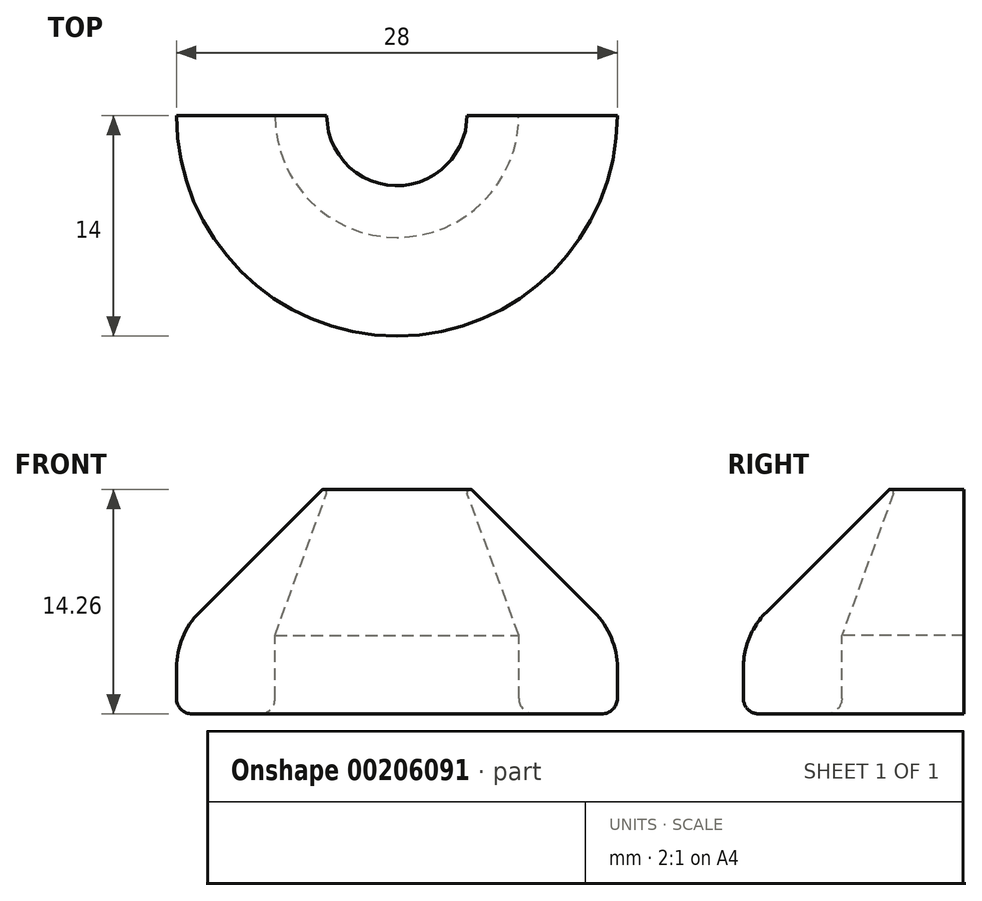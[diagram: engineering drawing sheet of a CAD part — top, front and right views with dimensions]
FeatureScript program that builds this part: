
annotation { "Feature Type Name" : "Feature", "Feature Type Description" : "" }
export const myFeature = defineFeature(function(context is Context, id is Id, definition is map)
    precondition{}
    {
        {
            var Q0;
            Q0=qCreatedBy(makeId("Front.planeOp"),FACE);
            var sketch = newSketch(context, id + "F0", { "sketchPlane" : qUnion([Q0])});
            skLineSegment(sketch, "E0", {"start": v(0, 30) * mm, "end": v(0, -30) * mm, "construction": true});
            skLineSegment(sketch, "E1", {"start": v(0, -30) * mm, "end": v(7.64, -30) * mm, "construction": true});
            skLineSegment(sketch, "E2", {"start": v(7.64, -30) * mm, "end": v(7.64, -25) * mm, "construction": true});
            skLineSegment(sketch, "E3", {"start": v(7.64, -25) * mm, "end": v(4, -15) * mm, "construction": true});
            skLineSegment(sketch, "E4", {"start": v(4, -15) * mm, "end": v(4, 0) * mm, "construction": true});
            skLineSegment(sketch, "E5", {"start": v(4, 0) * mm, "end": v(4, 15) * mm, "construction": true});
            skLineSegment(sketch, "E6", {"start": v(4, 15) * mm, "end": v(7.64, 25) * mm, "construction": true});
            skLineSegment(sketch, "E7", {"start": v(7.64, 25) * mm, "end": v(7.64, 30) * mm, "construction": true});
            skLineSegment(sketch, "E8", {"start": v(7.64, 30) * mm, "end": v(0, 30) * mm, "construction": true});
            skLineSegment(sketch, "E9", {"start": v(4, -15) * mm, "end": v(14, -25) * mm});
            skLineSegment(sketch, "E10", {"start": v(14, -25) * mm, "end": v(14, -30) * mm});
            skLineSegment(sketch, "E11", {"start": v(14, -30) * mm, "end": v(7.64, -30) * mm});
            skLineSegment(sketch, "E12", {"start": v(7.74, -30) * mm, "end": v(7.74, -25) * mm});
            skLineSegment(sketch, "E13", {"start": v(7.74, -25) * mm, "end": v(4.16, -15.16) * mm});
            skSolve(sketch);
        }
        {
            var Q0;
            Q0=qSketchRegion(id+"F0",true);
            var Q1;
            Q1=sQuery(id+"F0.wireOp",EDGE,"E0");
            revolve(context, id + "F1", {"entities" : qUnion([Q0]), "axis" : qUnion([Q1]), "revolveType" : RevolveType.ONE_DIRECTION, "angle" : 180 * degree});
        }
        {
            var Q0;
            Q0=makeQuery(id+"F1.opRevolve","SWEPT_EDGE",EDGE,{"disambiguationData":[OSD([sQuery(id+"F0.wireOp",EDGE,"E6"),sQuery(id+"F0.wireOp",EDGE,"E7")])]});
            var Q1;
            Q1=makeQuery(id+"F1.opRevolve","SWEPT_EDGE",EDGE,{"disambiguationData":[OSD([sQuery(id+"F0.wireOp",EDGE,"E2"),sQuery(id+"F0.wireOp",EDGE,"E3")])]});
            var Q2;
            Q2=makeQuery(id+"F1.opRevolve","SWEPT_EDGE",EDGE,{"disambiguationData":[OSD([sQuery(id+"F0.wireOp",EDGE,"E9"),sQuery(id+"F0.wireOp",EDGE,"E10")])]});
            fillet(context, id + "F2", {"entities" : qUnion([Q0, Q1, Q2]), "radius" : 5 * mm, "tangentPropagation" : true, "allowEdgeOverflow" : false});
        }
        {
            var Q0;
            Q0=makeQuery(id+"F1.opRevolve","SWEPT_EDGE",EDGE,{"disambiguationData":[OSD([sQuery(id+"F0.wireOp",EDGE,"E10"),sQuery(id+"F0.wireOp",EDGE,"E11")])]});
            var Q1;
            Q1=makeQuery(id+"F1.opRevolve","SWEPT_EDGE",EDGE,{"disambiguationData":[OSD([sQuery(id+"F0.wireOp",EDGE,"E11"),sQuery(id+"F0.wireOp",EDGE,"E12")])]});
            fillet(context, id + "F3", {"entities" : qUnion([Q0, Q1]), "radius" : 1 * mm, "tangentPropagation" : true, "allowEdgeOverflow" : false});
        }
        {
            var Q0;
            Q0=makeQuery(id+"F1.opRevolve","SWEPT_EDGE",EDGE,{"disambiguationData":[OSD([sQuery(id+"F0.wireOp",EDGE,"E9"),sQuery(id+"F0.wireOp",EDGE,"E13")])]});
            fillet(context, id + "F4", {"entities" : qUnion([Q0]), "radius" : .2 * mm, "tangentPropagation" : true, "allowEdgeOverflow" : false});
        }
    });
